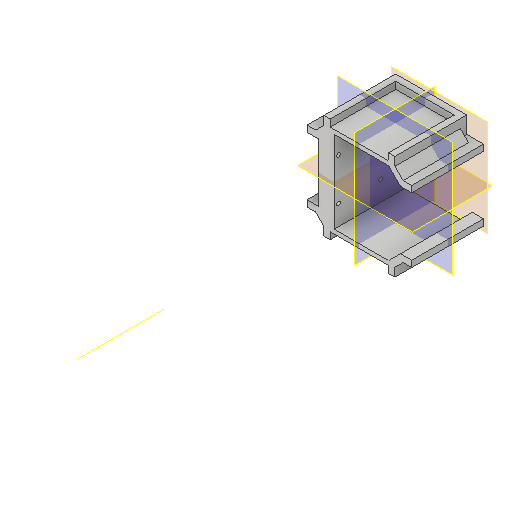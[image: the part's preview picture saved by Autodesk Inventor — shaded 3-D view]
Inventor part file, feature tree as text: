
AUTODESK INVENTOR PART (.ipt)
format: ipt  version: 2022 (Build 260153000, 153)  size: 270,848 bytes
history: native  units: mm
features: reference x14, other x11, plane x5, extrude x4, sketch x4, projected_geometry x3, chamfer x1, pattern_circular x1, hole x1
ambient origin geometry x8: Origin, YZ Plane, XZ Plane, XY Plane, X Axis, Y Axis, Z Axis, Center Point
bodies: Solid1 (feature_tree)
feature tree (44):
  plane  "Work Plane1"
  extrude  "Extrusion1"  Depth=3.0mm
  chamfer  "Chamfer1"  Distance=3.0mm
  sketch  "Sketch2"  dims[d6=3.0mm d7=3.0mm d8=3.0mm d9=0.0mm]
  plane  "Work Plane2"
  extrude  "Extrusion2"  Depth=3.001102mm
  other  "Work Axis1"
  pattern_circular  "Circular Pattern1"  Count=4 Angle=360.0deg
  plane  "Work Plane9"
  plane  "Work Plane10"
  plane  "Work Plane11"
  extrude  "Extrusion19"  Depth=2.0mm
  hole  "Hole4"  [1 undecoded]
  extrude  "Extrusion20"  Depth=3.0mm
  projected_geometry  "Projected Loop1"
  reference  "Reference42"
  reference  "Reference43"
  reference  "Reference44"
  reference  "Reference45"
  reference  "Reference46"
  sketch  "Sketch23"  dims[d10=3.9mm d11=2.0mm d12=45.0deg d13=3.001102mm]
  projected_geometry  "Projected Loop15"
  reference  "Reference47"
  reference  "Reference48"
  sketch  "Sketch24"  dims[d14=31.1mm d15=0.0mm d16=40.0mm d17=360.0deg]
  reference  "Reference49"
  reference  "Reference50"
  reference  "Reference51"
  reference  "Reference52"
  reference  "Reference53"
  reference  "Reference54"
  reference  "Reference55"
  sketch  "Sketch25"  dims[d112=3.0mm d113=0.0mm d114=2.0mm d115=2.0mm d116=1.8mm d117=6.0mm d118=6.5mm d119=3.0mm d120=90.0deg d121=15.0mm d122=20.594885mm d123=18.5mm d124=0.0mm d125=0.0mm]
  projected_geometry  "Projected Loop16"
  other  "<userpath> Lab\Documents\UC2-INVENTOR-Git\uc2_v3\Assembly_Cube_SQUID_Z_Focus_v3.iam"
  other  "Assembly_Cube_SQUID_Z_Focus_v3.iam"
  other  "AMETEK-21H4U-2_5-0_75-12-ENC:1"
  other  "<userpath>\Documents\UC2-INVENTOR-Git\uc2_v3\Assembly_Cube_SQUID_Z_Focus_v3.iam"
  other  "00_X-axis_MX25-SC:1"
  other  "Assembly_Cube_empty_IM_v3:2"
  other  "10_Cube_1x1_IM:1"
  other  "Assembly_Cube_Z_Focus_MGN_NEMA_v3.iam"
  other  "Assembly_Cube_empty_IM_v3:1"
  other  "10_Cube_1x1_IM:2"
note: 1 required parameter value undecoded (feature->parameter linkage not recoverable at this tier; creation-order binding heuristic only, values carry confidence <= 0.55)
